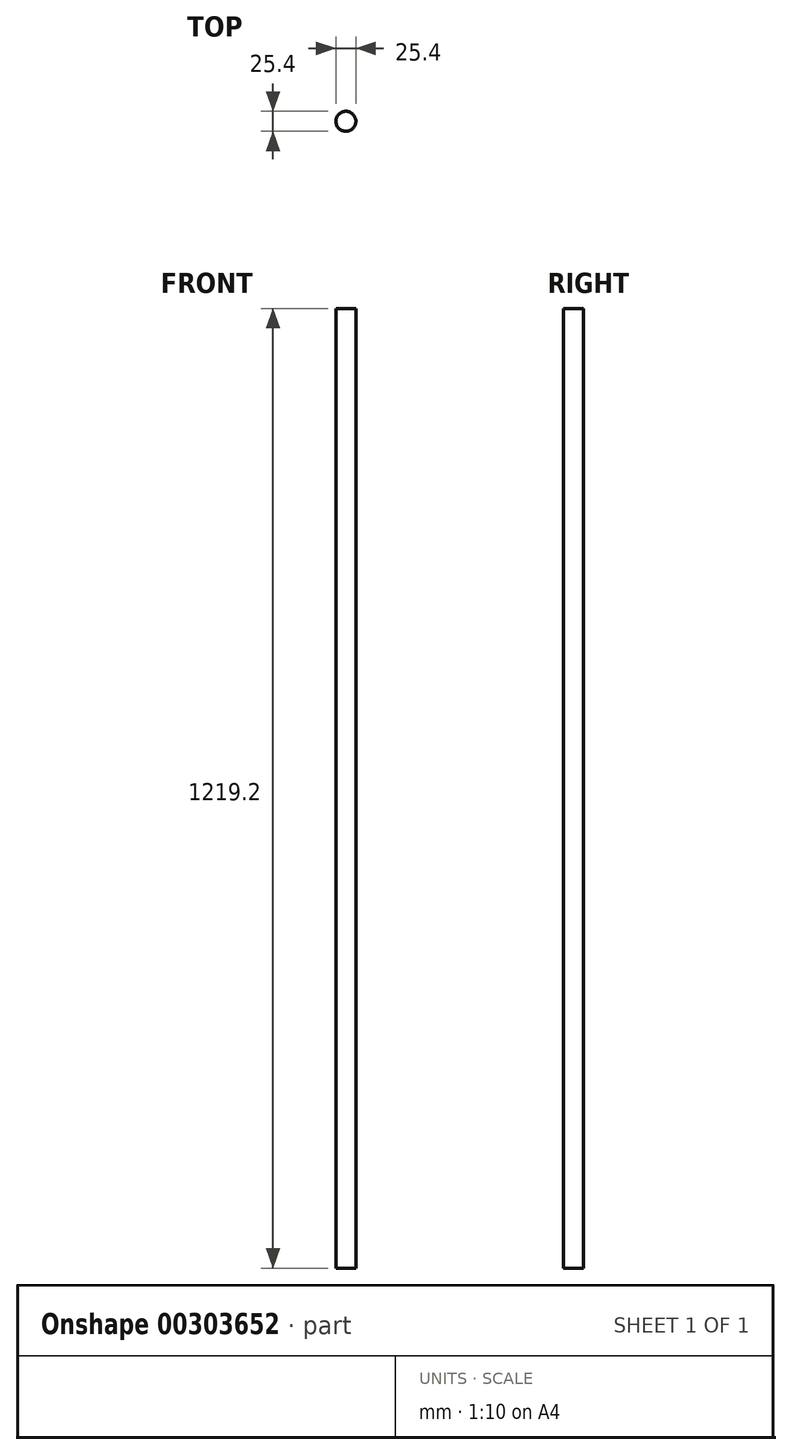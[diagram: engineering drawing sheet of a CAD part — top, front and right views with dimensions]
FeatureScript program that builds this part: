
annotation { "Feature Type Name" : "Feature", "Feature Type Description" : "" }
export const myFeature = defineFeature(function(context is Context, id is Id, definition is map)
    precondition{}
    {
        {
            var Q0;
            Q0=qCreatedBy(makeId("Front.planeOp"),FACE);
            var sketch = newSketch(context, id + "F0", { "sketchPlane" : qUnion([Q0])});
            skLineSegment(sketch, "E0", {"start": v(0, -73.32) * mm, "end": v(0, 1145.88) * mm});
            skLineSegment(sketch, "E1", {"start": v(0, 1145.88) * mm, "end": v(12.7, 1145.88) * mm});
            skLineSegment(sketch, "E2", {"start": v(12.7, 1145.88) * mm, "end": v(12.7, -73.32) * mm});
            skLineSegment(sketch, "E3", {"start": v(0, -73.32) * mm, "end": v(12.7, -73.32) * mm});
            skSolve(sketch);
        }
        {
            var Q0;
            Q0=makeQuery(id+"F0.imprint","IMPRINT",FACE,{"disambiguationData":[TD([[makeQuery(id+"F0.imprint","IMPRINT",EDGE,{"derivedFrom":sQuery(id+"F0.wireOp",EDGE,"E0")}),-1.0]])]});
            var Q1;
            Q1=sQuery(id+"F0.wireOp",EDGE,"E0");
            revolve(context, id + "F1", {"entities" : qUnion([Q0]), "axis" : qUnion([Q1]), "revolveType" : RevolveType.FULL});
        }
    });
